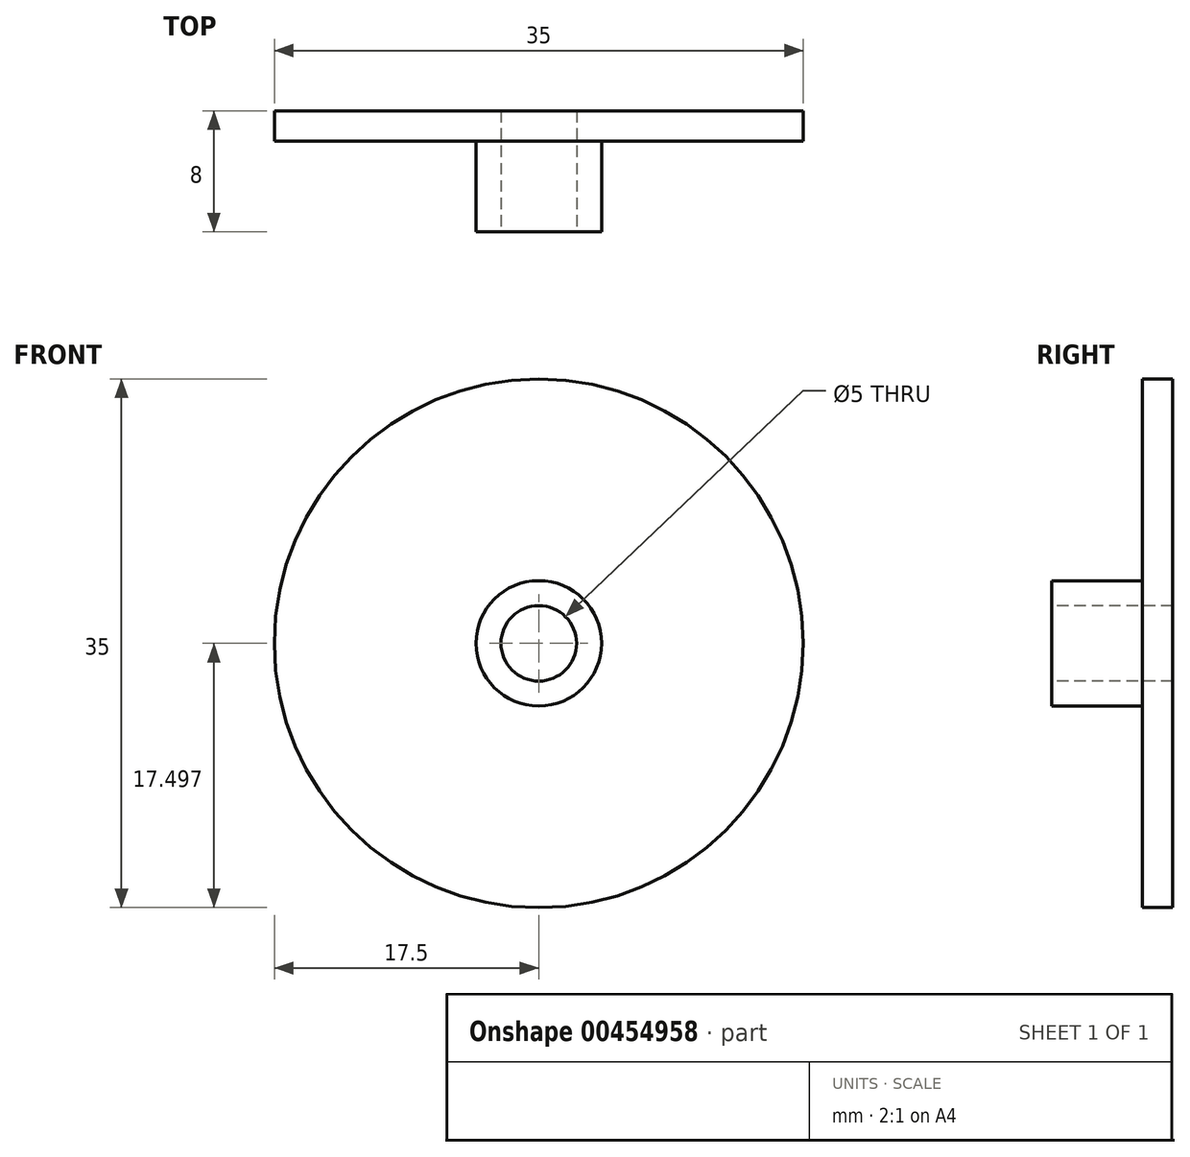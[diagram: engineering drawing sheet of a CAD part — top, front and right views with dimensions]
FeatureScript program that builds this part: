
annotation { "Feature Type Name" : "Feature", "Feature Type Description" : "" }
export const myFeature = defineFeature(function(context is Context, id is Id, definition is map)
    precondition{}
    {
        {
            var Q0;
            Q0=qCreatedBy(makeId("Front.planeOp"),FACE);
            var sketch = newSketch(context, id + "F0", { "sketchPlane" : qUnion([Q0])});
            skCircle(sketch, "E0", {"center": v(-15.67, 19.36) * mm, "radius": 17.5 * mm});
            skSolve(sketch);
        }
        {
            var Q0;
            Q0 = qSketchRegion(id + "F0", true);
            extrude(context, id + "F1", {"entities" : qUnion([Q0]), "depth" : 2 * mm});
        }
        {
            var Q0;
            Q0=makeQuery(id+"F1.opExtrude","CAP_FACE",FACE,{"disambiguationData":[OSD([sQuery(id+"F0.wireOp",EDGE,"E0")])],"isStart":false});
            var sketch = newSketch(context, id + "F2", { "sketchPlane" : qUnion([Q0])});
            skCircle(sketch, "E1", {"center": v(-15.67, 19.36) * mm, "radius": 2.5 * mm});
            skSolve(sketch);
        }
        {
            var Q0;
            Q0=makeQuery(id+"F2.imprint","IMPRINT",FACE,{"disambiguationData":[TD([[makeQuery(id+"F2.imprint","IMPRINT",EDGE,{"derivedFrom":sQuery(id+"F2.wireOp",EDGE,"E1")}),1.0]])]});
            var Q1;
            Q1 = qSketchRegion(id + "F9", true);
            extrude(context, id + "F3", {"entities" : qUnion([Q0, Q1]), "operationType" : NewBodyOperationType.ADD, "depth" : 6 * mm});
        }
        {
            var Q0;
            Q0=makeQuery(id+"F1.opExtrude","CAP_FACE",FACE,{"disambiguationData":[OSD([sQuery(id+"F0.wireOp",EDGE,"E0")])],"isStart":true});
            var sketch = newSketch(context, id + "F4", { "sketchPlane" : qUnion([Q0])});
            skCircle(sketch, "E2", {"center": v(15.67, 19.36) * mm, "radius": 2.5 * mm});
            skSolve(sketch);
        }
        {
            var Q0;
            Q0 = qSketchRegion(id + "F4", true);
            extrude(context, id + "F5", {"entities" : qUnion([Q0]), "operationType" : NewBodyOperationType.ADD, "depth" : 6 * mm});
        }
        {
            var Q0;
            Q0=makeQuery(id+"F3.opExtrude","CAP_FACE",FACE,{"disambiguationData":[OSD([sQuery(id+"F2.wireOp",EDGE,"E1")])],"isStart":false});
            extrude(context, id + "F6", {"entities" : qUnion([Q0]), "operationType" : NewBodyOperationType.REMOVE, "endBound" : BoundingType.THROUGH_ALL, "oppositeDirection" : true, "depth" : 25.4 * mm});
        }
        {
            var Q0;
            Q0=makeQuery(id+"F1.opExtrude","CAP_FACE",FACE,{"disambiguationData":[OSD([sQuery(id+"F0.wireOp",EDGE,"E0")])],"isStart":false});
            var sketch = newSketch(context, id + "F7", { "sketchPlane" : qUnion([Q0])});
            skCircle(sketch, "E3", {"center": v(-15.67, 19.36) * mm, "radius": 4.15 * mm});
            skSolve(sketch);
        }
        {
            var Q0;
            Q0=makeQuery(id+"F7.imprint","IMPRINT",FACE,{"disambiguationData":[TD([[makeQuery(id+"F7.imprint","IMPRINT",EDGE,{"derivedFrom":sQuery(id+"F7.wireOp",EDGE,"E3")}),1.0]])]});
            extrude(context, id + "F8", {"entities" : qUnion([Q0]), "operationType" : NewBodyOperationType.ADD, "depth" : 6 * mm});
        }
        {
            var Q0;
            Q0=makeQuery(id+"F1.opExtrude","CAP_FACE",FACE,{"disambiguationData":[OSD([sQuery(id+"F0.wireOp",EDGE,"E0")])],"isStart":true});
            var sketch = newSketch(context, id + "F9", { "sketchPlane" : qUnion([Q0])});
            skCircle(sketch, "E4", {"center": v(15.67, 19.36) * mm, "radius": 3.04 * mm});
            skSolve(sketch);
        }
        {
            var Q0;
            Q0=makeQuery(id+"F9.imprint","IMPRINT",FACE,{"disambiguationData":[TD([[makeQuery(id+"F9.imprint","IMPRINT",EDGE,{"derivedFrom":sQuery(id+"F9.wireOp",EDGE,"E4")}),-1.0]])]});
            var sketch = newSketch(context, id + "F10", { "sketchPlane" : qUnion([Q0])});
            skCircle(sketch, "E5", {"center": v(15.67, 19.36) * mm, "radius": 4.24 * mm});
            skSolve(sketch);
        }
        {
            var Q0;
            Q0=sQuery(id+"F10.wireOp",EDGE,"E5");
            extrude(context, id + "F11", {"bodyType" : ToolBodyType.SURFACE, "surfaceEntities" : qUnion([Q0]), "depth" : 5 * mm});
        }
    });
